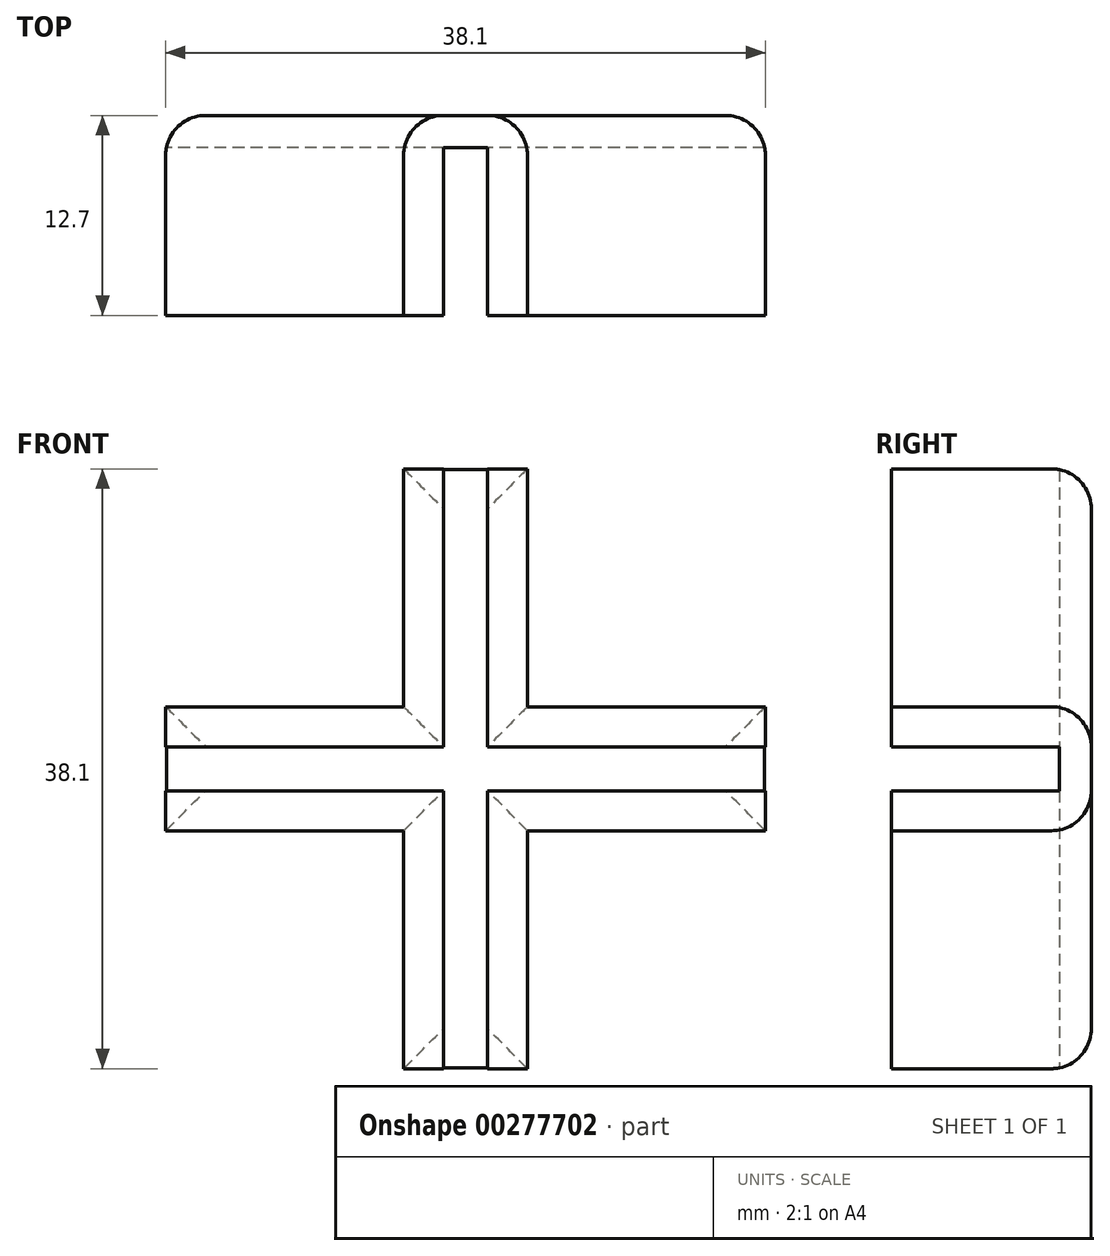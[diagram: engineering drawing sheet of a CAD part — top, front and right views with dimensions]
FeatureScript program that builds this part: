
annotation { "Feature Type Name" : "Feature", "Feature Type Description" : "" }
export const myFeature = defineFeature(function(context is Context, id is Id, definition is map)
    precondition{}
    {
        {
            var Q0;
            Q0=qCreatedBy(makeId("Front.planeOp"),FACE);
            var sketch = newSketch(context, id + "F0", { "sketchPlane" : qUnion([Q0])});
            skLineSegment(sketch, "E0.bottom", {"start": v(-19.05, 19.05) * mm, "end": v(19.05, 19.05) * mm, "construction": true});
            skLineSegment(sketch, "E0.top", {"start": v(-19.05, -19.05) * mm, "end": v(19.05, -19.05) * mm, "construction": true});
            skLineSegment(sketch, "E0.left", {"start": v(-19.05, 19.05) * mm, "end": v(-19.05, -19.05) * mm, "construction": true});
            skLineSegment(sketch, "E0.right", {"start": v(19.05, 19.05) * mm, "end": v(19.05, -19.05) * mm, "construction": true});
            skPoint(sketch, "E0.middle", {"position": v(0, 0) * mm});
            skLineSegment(sketch, "E1.bottom", {"start": v(-3.94, 19.05) * mm, "end": v(3.94, 19.05) * mm});
            skLineSegment(sketch, "E1.top", {"start": v(-3.94, -19.05) * mm, "end": v(3.94, -19.05) * mm});
            skLineSegment(sketch, "E1.left", {"start": v(-3.94, 19.05) * mm, "end": v(-3.94, 3.94) * mm});
            skLineSegment(sketch, "E1.right", {"start": v(3.94, 19.05) * mm, "end": v(3.94, 3.94) * mm});
            skLineSegment(sketch, "E2.bottom", {"start": v(-19.05, 3.94) * mm, "end": v(-3.94, 3.94) * mm});
            skLineSegment(sketch, "E2.top", {"start": v(-19.05, -3.94) * mm, "end": v(-3.94, -3.94) * mm});
            skLineSegment(sketch, "E2.left", {"start": v(-19.05, 3.94) * mm, "end": v(-19.05, -3.94) * mm});
            skLineSegment(sketch, "E2.right", {"start": v(19.05, 3.94) * mm, "end": v(19.05, -3.94) * mm});
            skLineSegment(sketch, "E3.trimOffspring", {"start": v(3.94, 3.94) * mm, "end": v(19.05, 3.94) * mm});
            skLineSegment(sketch, "E4.trimOffspring", {"start": v(-3.94, -3.94) * mm, "end": v(-3.94, -19.05) * mm});
            skLineSegment(sketch, "E5.trimOffspring", {"start": v(3.94, -3.94) * mm, "end": v(19.05, -3.94) * mm});
            skLineSegment(sketch, "E6.trimOffspring", {"start": v(3.94, -3.94) * mm, "end": v(3.94, -19.05) * mm});
            skLineSegment(sketch, "E7", {"start": v(-1.4, 19.05) * mm, "end": v(-1.4, 1.4) * mm});
            skLineSegment(sketch, "E8", {"start": v(-1.4, 1.4) * mm, "end": v(-19.05, 1.4) * mm});
            skPoint(sketch, "E8.endSnap0", {"position": v(-19.05, 0) * mm});
            skLineSegment(sketch, "E9", {"start": v(-19.05, 1.4) * mm, "end": v(-19.05, -1.4) * mm});
            skLineSegment(sketch, "E10", {"start": v(-19.05, -1.4) * mm, "end": v(-1.4, -1.4) * mm});
            skLineSegment(sketch, "E11", {"start": v(-1.4, -1.4) * mm, "end": v(-1.4, -19.05) * mm});
            skLineSegment(sketch, "E12", {"start": v(1.4, 19.05) * mm, "end": v(1.4, 1.4) * mm});
            skLineSegment(sketch, "E13", {"start": v(1.4, 1.4) * mm, "end": v(19.05, 1.4) * mm});
            skLineSegment(sketch, "E14", {"start": v(19.05, 1.4) * mm, "end": v(19.05, -1.4) * mm});
            skLineSegment(sketch, "E15", {"start": v(19.05, -1.4) * mm, "end": v(1.4, -1.4) * mm});
            skLineSegment(sketch, "E16", {"start": v(1.4, -1.4) * mm, "end": v(1.4, -19.05) * mm});
            skSolve(sketch);
        }
        {
            var Q0;
            {var subQ2=sQuery(id+"F0.wireOp",EDGE,"E7");Q0=makeQuery(id+"F0.imprint","IMPRINT",FACE,{"disambiguationData":[TD([[makeQuery(id+"F0.imprint","IMPRINT",EDGE,{"derivedFrom":subQ2}),1.0]])]});}
            extrude(context, id + "F1", {"entities" : qUnion([Q0]), "depth" : 2.03 * mm});
        }
        {
            var Q0;
            {var subQ3=sQuery(id+"F0.wireOp",EDGE,"E1.left");Q0=makeQuery(id+"F0.imprint","IMPRINT",FACE,{"disambiguationData":[TD([[makeQuery(id+"F0.imprint","IMPRINT",EDGE,{"derivedFrom":subQ3}),1.0]])]});}
            var Q1;
            {var subQ1=sQuery(id+"F0.wireOp",EDGE,"E1.right");Q1=makeQuery(id+"F0.imprint","IMPRINT",FACE,{"disambiguationData":[TD([[makeQuery(id+"F0.imprint","IMPRINT",EDGE,{"derivedFrom":subQ1}),-1.0]])]});}
            var Q2;
            {var subQ2=sQuery(id+"F0.wireOp",EDGE,"E2.top");Q2=makeQuery(id+"F0.imprint","IMPRINT",FACE,{"disambiguationData":[TD([[makeQuery(id+"F0.imprint","IMPRINT",EDGE,{"derivedFrom":subQ2}),1.0]])]});}
            var Q3;
            {var subQ1=sQuery(id+"F0.wireOp",EDGE,"E5.trimOffspring");Q3=makeQuery(id+"F0.imprint","IMPRINT",FACE,{"disambiguationData":[TD([[makeQuery(id+"F0.imprint","IMPRINT",EDGE,{"derivedFrom":subQ1}),1.0]])]});}
            extrude(context, id + "F2", {"entities" : qUnion([Q0, Q1, Q2, Q3]), "operationType" : NewBodyOperationType.ADD, "depth" : 12.7 * mm});
        }
        {
            var Q0;
            {var subQ0=sQuery(id+"F0.wireOp",EDGE,"E16");var subQ1=sQuery(id+"F0.wireOp",EDGE,"E15");var subQ2=sQuery(id+"F0.wireOp",EDGE,"E2.right");var subQ3=sQuery(id+"F0.wireOp",EDGE,"E1.top");var subQ4=sQuery(id+"F0.wireOp",EDGE,"E11");var subQ5=sQuery(id+"F0.wireOp",EDGE,"E10");var subQ6=sQuery(id+"F0.wireOp",EDGE,"E2.left");var subQ7=sQuery(id+"F0.wireOp",EDGE,"E13");var subQ8=sQuery(id+"F0.wireOp",EDGE,"E12");var subQ9=sQuery(id+"F0.wireOp",EDGE,"E1.bottom");var subQ10=sQuery(id+"F0.wireOp",EDGE,"E8");var subQ11=sQuery(id+"F0.wireOp",EDGE,"E7");Q0=makeQuery(id+"F2.boolean.opBoolean","MERGE",FACE,{"derivedFrom":[makeQuery(id+"F1.opExtrude","CAP_FACE",FACE,{"disambiguationData":[OSD([subQ9,subQ3,subQ11,subQ10,sQuery(id+"F0.wireOp",EDGE,"E9"),subQ5,subQ4,subQ8,subQ7,sQuery(id+"F0.wireOp",EDGE,"E14"),subQ1,subQ0])],"isStart":true}),makeQuery(id+"F2.opExtrude","CAP_FACE",FACE,{"disambiguationData":[OSD([subQ9,sQuery(id+"F0.wireOp",EDGE,"E1.left"),sQuery(id+"F0.wireOp",EDGE,"E2.bottom"),subQ6,subQ11,subQ10])],"isStart":true}),makeQuery(id+"F2.opExtrude","CAP_FACE",FACE,{"disambiguationData":[OSD([subQ9,sQuery(id+"F0.wireOp",EDGE,"E1.right"),subQ2,sQuery(id+"F0.wireOp",EDGE,"E3.trimOffspring"),subQ8,subQ7])],"isStart":true}),makeQuery(id+"F2.opExtrude","CAP_FACE",FACE,{"disambiguationData":[OSD([subQ3,sQuery(id+"F0.wireOp",EDGE,"E2.top"),subQ6,sQuery(id+"F0.wireOp",EDGE,"E4.trimOffspring"),subQ5,subQ4])],"isStart":true}),makeQuery(id+"F2.opExtrude","CAP_FACE",FACE,{"disambiguationData":[OSD([subQ3,subQ2,sQuery(id+"F0.wireOp",EDGE,"E5.trimOffspring"),sQuery(id+"F0.wireOp",EDGE,"E6.trimOffspring"),subQ1,subQ0])],"isStart":true})]});}
            fillet(context, id + "F3", {"entities" : qUnion([Q0]), "radius" : 2.54 * mm, "tangentPropagation" : true, "allowEdgeOverflow" : false});
        }
    });
